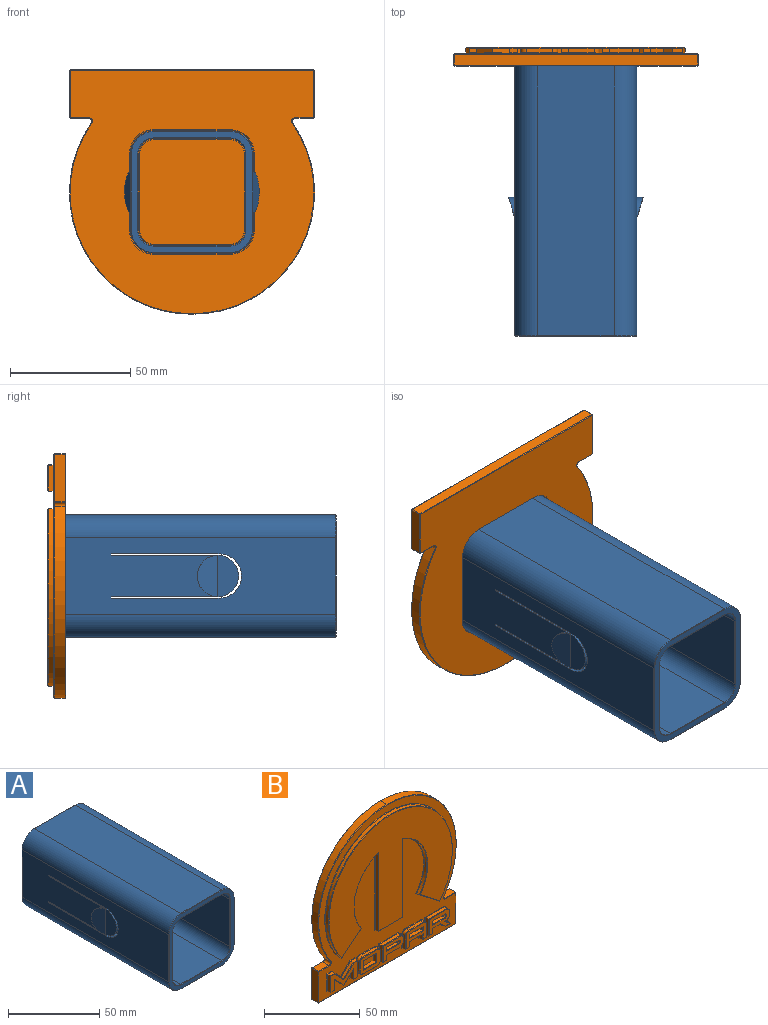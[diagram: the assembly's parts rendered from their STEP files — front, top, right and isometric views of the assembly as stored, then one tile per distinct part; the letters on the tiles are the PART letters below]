
ASSEMBLY  parts=2 mates=1
PART A: 72 faces, bbox 61x119.4x55.9 mm
  f0: cylinder r=8.57mm len=17.15mm, axis (1,0,0), area 0mm2, adj f6,f39
  f1: plane 17.15x8.58mm, normal (-1,0,0), area 115.4mm2, adj f23,f39
  f2: plane 113.79x31.75mm, normal (1,0,0), area 3296.9mm2, adj f9,f18,f29,f30,f31,f32,f33,f35
  f3: plane 17.15x8.58mm, normal (1,0,0), area 115.4mm2, adj f34,f38
  f4: plane 113.79x31.75mm, normal (0,0,1), area 3612.9mm2, adj f5,f18,f47,f63
  f5: cylinder r=9.53mm len=113.79mm, axis (0,1,0), area 1702.5mm2, adj f4,f6,f46,f62
  f6: plane 113.79x31.75mm, normal (-1,0,0), area 3296.9mm2, adj f0,f5,f7,f21,f22,f24,f25,f26
  f7: cylinder r=9.53mm len=113.79mm, axis (0,1,0), area 1702.5mm2, adj f6,f8,f42,f58
  f8: plane 113.79x31.75mm, normal (0,0,-1), area 3612.9mm2, adj f7,f9,f40,f56
  f9: cylinder r=9.53mm len=113.79mm, axis (0,1,0), area 1702.5mm2, adj f2,f8,f41,f57
  f10: cylinder r=6.35mm len=113.79mm, axis (0,1,0), area 1135mm2, adj f11,f17,f48,f64
  f11: plane 113.79x31.75mm, normal (-1,0,0), area 3527.8mm2, adj f10,f12,f29,f30,f31,f32,f33,f34
  f12: cylinder r=6.35mm len=113.79mm, axis (0,1,0), area 1135mm2, adj f11,f13,f52,f68
  f13: plane 113.79x31.75mm, normal (0,0,1), area 3612.9mm2, adj f12,f14,f54,f70
  f14: cylinder r=6.35mm len=113.79mm, axis (0,1,0), area 1135mm2, adj f13,f15,f55,f71
  f15: plane 113.79x31.75mm, normal (1,0,0), area 3527.8mm2, adj f14,f16,f21,f22,f23,f24,f25,f26
  f16: cylinder r=6.35mm len=113.79mm, axis (0,1,0), area 1135mm2, adj f15,f17,f51,f67
  f17: plane 113.79x31.75mm, normal (0,0,-1), area 3612.9mm2, adj f10,f16,f49,f65
  f18: cylinder r=9.53mm len=113.79mm, axis (0,1,0), area 1702.5mm2, adj f2,f4,f45,f61
  f19: plane 50.29x50.29mm, normal (0,-1,0), area 471.7mm2, adj f56,f57,f58,f59,f60,f61,f62,f63
  f20: plane 50.29x50.29mm, normal (0,1,0), area 471.7mm2, adj f40,f41,f42,f43,f44,f45,f46,f47
  f21: plane 3.18x0.64mm, normal (0,-1,0), area 2mm2, adj f6,f15,f22,f28
  f22: plane 44.45x3.18mm, normal (0,0,1), area 141.1mm2, adj f6,f15,f21,f23
  f23: cylinder r=8.57mm len=17.15mm, axis (1,0,0), area 85.6mm2, adj f1,f15,f22,f24
  f24: plane 44.45x3.18mm, normal (0,0,-1), area 141.1mm2, adj f6,f15,f23,f25
  f25: plane 3.18x0.64mm, normal (0,-1,0), area 2mm2, adj f6,f15,f24,f26
  f26: plane 44.45x3.18mm, normal (0,0,1), area 141.1mm2, adj f6,f15,f25,f27
  f27: cylinder r=9.22mm len=18.45mm, axis (1,0,0), area 95.6mm2, adj f6,f15,f26,f28
  f28: plane 44.45x3.18mm, normal (0,0,-1), area 141.1mm2, adj f6,f15,f21,f27
  f29: plane 44.45x3.18mm, normal (0,0,-1), area 141.1mm2, adj f2,f11,f30,f36
  f30: cylinder r=9.22mm len=18.45mm, axis (1,0,0), area 95.6mm2, adj f2,f11,f29,f31
  f31: plane 44.45x3.18mm, normal (0,0,1), area 141.1mm2, adj f2,f11,f30,f32
  f32: plane 3.18x0.64mm, normal (0,-1,0), area 2mm2, adj f2,f11,f31,f33
  f33: plane 44.45x3.18mm, normal (0,0,-1), area 141.1mm2, adj f2,f11,f32,f34
  f34: cylinder r=8.57mm len=17.15mm, axis (1,0,0), area 85.6mm2, adj f3,f11,f33,f35
  f35: plane 44.45x3.18mm, normal (0,0,1), area 141.1mm2, adj f2,f11,f34,f36
  f36: plane 3.18x0.64mm, normal (0,-1,0), area 2mm2, adj f2,f11,f29,f35
  f37: cylinder r=8.57mm len=17.15mm, axis (-1,0,0), area 0mm2, adj f2,f38
  f38: plane 22.22x13.65mm, normal (0.96,-0.28,0), area 120.4mm2, adj f3,f37
  f39: plane 22.22x13.65mm, normal (-0.96,-0.28,0), area 120.4mm2, adj f0,f1
  f40: plane 31.75x0.25mm, normal (0,0.71,-0.71), area 11.4mm2, adj f8,f20,f41,f42
  f41: cone r=9.53mm half-angle=45deg, axis (0,-1,0), area 5.3mm2, adj f9,f20,f40,f43
  f42: cone r=9.53mm half-angle=45deg, axis (0,-1,0), area 5.3mm2, adj f7,f20,f40,f44
  f43: plane 31.75x0.25mm, normal (0.71,0.71,0), area 11.4mm2, adj f2,f20,f41,f45
  f44: plane 31.75x0.25mm, normal (-0.71,0.71,0), area 11.4mm2, adj f6,f20,f42,f46
  f45: cone r=9.53mm half-angle=45deg, axis (0,-1,0), area 5.3mm2, adj f18,f20,f43,f47
  f46: cone r=9.53mm half-angle=45deg, axis (0,-1,0), area 5.3mm2, adj f5,f20,f44,f47
  f47: plane 31.75x0.25mm, normal (0,0.71,0.71), area 11.4mm2, adj f4,f20,f45,f46
  f48: cone r=6.6mm half-angle=45deg, axis (0,1,0), area 3.7mm2, adj f10,f20,f49,f50
  f49: plane 31.75x0.25mm, normal (0,0.71,-0.71), area 11.4mm2, adj f17,f20,f48,f51
  f50: plane 31.75x0.25mm, normal (-0.71,0.71,0), area 11.4mm2, adj f11,f20,f48,f52
  f51: cone r=6.6mm half-angle=45deg, axis (0,1,0), area 3.7mm2, adj f16,f20,f49,f53
  f52: cone r=6.6mm half-angle=45deg, axis (0,1,0), area 3.7mm2, adj f12,f20,f50,f54
  f53: plane 31.75x0.25mm, normal (0.71,0.71,0), area 11.4mm2, adj f15,f20,f51,f55
  f54: plane 31.75x0.25mm, normal (0,0.71,0.71), area 11.4mm2, adj f13,f20,f52,f55
  f55: cone r=6.6mm half-angle=45deg, axis (0,1,0), area 3.7mm2, adj f14,f20,f53,f54
  f56: plane 31.75x0.25mm, normal (0,-0.71,-0.71), area 11.4mm2, adj f8,f19,f57,f58
  f57: cone r=9.27mm half-angle=45deg, axis (0,1,0), area 5.3mm2, adj f9,f19,f56,f59
  f58: cone r=9.27mm half-angle=45deg, axis (0,1,0), area 5.3mm2, adj f7,f19,f56,f60
  f59: plane 31.75x0.25mm, normal (0.71,-0.71,0), area 11.4mm2, adj f2,f19,f57,f61
  f60: plane 31.75x0.25mm, normal (-0.71,-0.71,0), area 11.4mm2, adj f6,f19,f58,f62
  f61: cone r=9.27mm half-angle=45deg, axis (0,1,0), area 5.3mm2, adj f18,f19,f59,f63
  f62: cone r=9.27mm half-angle=45deg, axis (0,1,0), area 5.3mm2, adj f5,f19,f60,f63
  f63: plane 31.75x0.25mm, normal (0,-0.71,0.71), area 11.4mm2, adj f4,f19,f61,f62
  f64: cone r=6.35mm half-angle=45deg, axis (0,-1,0), area 3.7mm2, adj f10,f19,f65,f66
  f65: plane 31.75x0.25mm, normal (0,-0.71,-0.71), area 11.4mm2, adj f17,f19,f64,f67
  f66: plane 31.75x0.25mm, normal (-0.71,-0.71,0), area 11.4mm2, adj f11,f19,f64,f68
  f67: cone r=6.35mm half-angle=45deg, axis (0,-1,0), area 3.7mm2, adj f16,f19,f65,f69
  f68: cone r=6.35mm half-angle=45deg, axis (0,-1,0), area 3.7mm2, adj f12,f19,f66,f70
  f69: plane 31.75x0.25mm, normal (0.71,-0.71,0), area 11.4mm2, adj f15,f19,f67,f71
  f70: plane 31.75x0.25mm, normal (0,-0.71,0.71), area 11.4mm2, adj f13,f19,f68,f71
  f71: cone r=6.35mm half-angle=45deg, axis (0,-1,0), area 3.7mm2, adj f14,f19,f69,f70
PART B: 279 faces, bbox 101.9x7.6x101.6 mm
  f0: plane 101.38x101.09mm, normal (0,1,0), area 6348.8mm2, adj f110,f114,f115,f119,f123,f124,f128,f132
  f1: plane 101.38x101.09mm, normal (0,-1,0), area 4120.3mm2, adj f113,f117,f118,f122,f126,f127,f131,f134
  f2: plane 19.72x4.57mm, normal (-1,0,0), area 90.2mm2, adj f109,f115,f116,f117
  f3: plane 101.09x4.57mm, normal (0,0,-1), area 462.2mm2, adj f116,f124,f125,f126
  f4: plane 19.72x4.57mm, normal (1,0,0), area 90.2mm2, adj f125,f133,f134,f138
  f5: plane 7.75x4.57mm, normal (0,0,1), area 35.4mm2, adj f6,f132,f135,f138
  f6: cylinder r=1.14mm len=4.57mm, axis (0,-1,0), area 10.7mm2, adj f5,f7,f128,f131
  f7: cylinder r=50.6mm len=79.71mm, axis (0,-1,0), area 507mm2, adj f6,f8,f123,f127
  f8: cylinder r=50.59mm len=79.71mm, axis (0,-1,0), area 506.5mm2, adj f7,f9,f119,f122
  f9: cylinder r=1.21mm len=4.57mm, axis (0,-1,0), area 10.8mm2, adj f8,f10,f114,f118
  f10: plane 7.75x4.57mm, normal (0,0,1), area 35.4mm2, adj f9,f109,f110,f113
  f11: cylinder r=27.14mm len=41.92mm, axis (0,1,0), area 103.1mm2, adj f12,f18,f251,f259
  f12: plane 49.94x2.03mm, normal (-1,0,0), area 101.5mm2, adj f11,f13,f249,f257
  f13: plane 18.1x2.03mm, normal (0,0,-1), area 36.8mm2, adj f12,f14,f247,f255
  f14: plane 49.94x2.03mm, normal (1,0,0), area 101.5mm2, adj f13,f15,f248,f256
  f15: cylinder r=26.93mm len=41.92mm, axis (0,1,0), area 103.5mm2, adj f14,f16,f250,f258
  f16: plane 14.83x11.39mm, normal (-0.61,0,-0.79), area 38mm2, adj f15,f17,f252,f260
  f17: cylinder r=45.71mm len=91.43mm, axis (0,1,0), area 414.1mm2, adj f16,f18,f254,f262
  f18: plane 14.83x11.62mm, normal (0.62,0,-0.79), area 38.3mm2, adj f11,f17,f253,f261
  f19: plane 90.92x73.17mm, normal (0,-1,0), area 3840.9mm2, adj f255,f256,f257,f258,f259,f260,f261,f262
  f20: plane 10.61x2.03mm, normal (-1,0,0), area 21.6mm2, adj f21,f31,f199,f245
  f21: plane 3.08x2.03mm, normal (0,0,-1), area 6.3mm2, adj f20,f22,f200,f246
  f22: plane 6.64x2.03mm, normal (1,0,0), area 13.5mm2, adj f21,f23,f198,f244
  f23: plane 6.91x6.73mm, normal (-0.72,0,-0.7), area 19.6mm2, adj f22,f24,f196,f242
  f24: plane 7.1x6.91mm, normal (0.7,0,-0.72), area 20.1mm2, adj f23,f25,f194,f240
  f25: plane 6.64x2.03mm, normal (-1,0,0), area 13.5mm2, adj f24,f26,f192,f238
  f26: plane 3.07x2.03mm, normal (0,0,-1), area 6.2mm2, adj f25,f27,f190,f236
  f27: plane 10.61x2.03mm, normal (1,0,0), area 21.6mm2, adj f26,f28,f189,f235
  f28: plane 3.12x2.03mm, normal (0,0,1), area 6.3mm2, adj f27,f29,f191,f237
  f29: plane 7.05x6.86mm, normal (-0.7,0,0.72), area 20mm2, adj f28,f30,f193,f239
  f30: plane 6.86x6.68mm, normal (0.72,0,0.7), area 19.5mm2, adj f29,f31,f195,f241
  f31: plane 3.13x2.03mm, normal (0,0,1), area 6.4mm2, adj f20,f30,f197,f243
  f32: plane 19.47x10.27mm, normal (0,-1,0), area 99.2mm2, adj f189,f190,f191,f192,f193,f194,f195,f196
  f33: plane 6.36x2.03mm, normal (1,0,0), area 12.9mm2, adj f34,f44,f183,f229
  f34: cylinder r=2.09mm len=2.23mm, axis (0,1,0), area 6.9mm2, adj f33,f35,f181,f227
  f35: plane 10.69x2.03mm, normal (0,0,1), area 21.7mm2, adj f34,f36,f182,f228
  f36: cylinder r=2.11mm len=2.42mm, axis (0,1,0), area 7.4mm2, adj f35,f37,f184,f230
  f37: plane 6.36x2.03mm, normal (-1,0,0), area 12.9mm2, adj f36,f38,f186,f232
  f38: cylinder r=2.31mm len=2.42mm, axis (0,1,0), area 7.6mm2, adj f37,f39,f188,f234
  f39: plane 10.69x2.03mm, normal (0,0,-1), area 21.7mm2, adj f38,f44,f187,f233
  f40: plane 5.47x2.29mm, normal (1,0,0), area 12.5mm2, adj f41,f43,f46,f179
  f41: plane 9.25x2.29mm, normal (0,0,-1), area 21.1mm2, adj f40,f42,f46,f180
  f42: plane 5.47x2.29mm, normal (-1,0,0), area 12.5mm2, adj f41,f43,f46,f178
  f43: plane 9.25x2.29mm, normal (0,0,1), area 21.1mm2, adj f40,f42,f46,f177
  f44: cylinder r=2.23mm len=2.31mm, axis (0,1,0), area 7.3mm2, adj f33,f39,f185,f231
  f45: plane 14.83x10.27mm, normal (0,-1,0), area 90.4mm2, adj f177,f178,f179,f180,f181,f182,f183,f184
  f46: plane 9.25x5.47mm, normal (0,-1,0), area 50.6mm2, adj f40,f41,f42,f43
  f47: plane 13.6x2.03mm, normal (0,0,1), area 27.6mm2, adj f48,f56,f175,f225
  f48: plane 10.75x2.03mm, normal (-1,0,0), area 21.8mm2, adj f47,f49,f173,f223
  f49: plane 3.01x2.03mm, normal (0,0,-1), area 6.1mm2, adj f48,f50,f171,f221
  f50: plane 3.3x2.03mm, normal (1,0,0), area 6.7mm2, adj f49,f51,f172,f222
  f51: plane 10.59x2.03mm, normal (0,0,-1), area 21.5mm2, adj f50,f56,f174,f224
  f52: plane 2.29x1.9mm, normal (1,0,0), area 4.3mm2, adj f53,f55,f58,f167
  f53: plane 9.26x2.29mm, normal (0,0,-1), area 21.2mm2, adj f52,f54,f58,f169
  f54: cylinder r=1.41mm len=2.29mm, axis (0,1,0), area 4.8mm2, adj f53,f55,f58,f170
  f55: plane 9.26x2.29mm, normal (0,0,1), area 21.2mm2, adj f52,f54,f58,f168
  f56: cylinder r=4.16mm len=7.45mm, axis (0,1,0), area 18.7mm2, adj f47,f51,f176,f226
  f57: plane 15.4x10.24mm, normal (0,-1,0), area 87mm2, adj f167,f168,f169,f170,f171,f172,f173,f174
  f58: plane 9.62x1.9mm, normal (0,-1,0), area 18mm2, adj f52,f53,f54,f55
  f59: plane 2.29x2.16mm, normal (1,0,0), area 4.9mm2, adj f60,f72,f74,f155
  f60: plane 9.3x2.29mm, normal (0,0,-1), area 21.3mm2, adj f59,f61,f74,f156
  f61: plane 2.29x2.16mm, normal (-1,0,0), area 4.9mm2, adj f60,f72,f74,f154
  f62: plane 8.63x2.03mm, normal (-1,0,0), area 17.5mm2, adj f63,f71,f161,f215
  f63: plane 3.1x2.03mm, normal (0,0,-1), area 6.3mm2, adj f62,f64,f159,f213
  f64: plane 3.37x2.03mm, normal (1,0,0), area 6.8mm2, adj f63,f65,f157,f211
  f65: plane 9.44x2.03mm, normal (0,0,-1), area 19.2mm2, adj f64,f66,f158,f212
  f66: plane 3.37x2.03mm, normal (-1,0,0), area 6.8mm2, adj f65,f67,f160,f214
  f67: plane 2.96x2.03mm, normal (0,0,-1), area 6mm2, adj f66,f68,f162,f216
  f68: plane 8.63x2.03mm, normal (1,0,0), area 17.5mm2, adj f67,f69,f164,f218
  f69: cylinder r=2.31mm len=2.31mm, axis (0,1,0), area 7mm2, adj f68,f70,f166,f220
  f70: plane 10.67x2.03mm, normal (0,0,1), area 21.7mm2, adj f69,f71,f165,f219
  f71: cylinder r=2.15mm len=2.52mm, axis (0,1,0), area 7.6mm2, adj f62,f70,f163,f217
  f72: plane 9.3x2.29mm, normal (0,0,1), area 21.3mm2, adj f59,f61,f74,f153
  f73: plane 14.99x10.27mm, normal (0,-1,0), area 92.2mm2, adj f153,f154,f155,f156,f157,f158,f159,f160
  f74: plane 9.3x2.16mm, normal (0,-1,0), area 20.1mm2, adj f59,f60,f61,f72
  f75: plane 13.4x2.03mm, normal (0,0,1), area 27.2mm2, adj f76,f88,f151,f209
  f76: plane 10.75x2.03mm, normal (-1,0,0), area 21.8mm2, adj f75,f77,f149,f207
  f77: plane 3.13x2.03mm, normal (0,0,-1), area 6.4mm2, adj f76,f78,f147,f205
  f78: plane 3.37x2.03mm, normal (1,0,0), area 6.8mm2, adj f77,f79,f145,f203
  f79: plane 5.28x2.03mm, normal (0,0,-1), area 10.7mm2, adj f78,f80,f143,f201
  f80: plane 3.87x3.37mm, normal (-0.66,0,-0.75), area 10.4mm2, adj f79,f81,f144,f202
  f81: plane 4.23x2.03mm, normal (0,0,-1), area 8.6mm2, adj f80,f82,f146,f204
  f82: plane 4.23x3.37mm, normal (0.62,0,0.78), area 11mm2, adj f81,f83,f148,f206
  f83: plane 2.03x1.13mm, normal (0,0,-1), area 2.3mm2, adj f82,f88,f150,f208
  f84: plane 2.29x2.16mm, normal (1,0,0), area 4.9mm2, adj f85,f87,f90,f139
  f85: plane 9.03x2.29mm, normal (0,0,-1), area 20.6mm2, adj f84,f86,f90,f141
  f86: cylinder r=1.19mm len=2.29mm, axis (0,1,0), area 6.2mm2, adj f85,f87,f90,f142
  f87: plane 9.03x2.29mm, normal (0,0,1), area 20.6mm2, adj f84,f86,f90,f140
  f88: cylinder r=4.03mm len=7.38mm, axis (0,1,0), area 19mm2, adj f75,f83,f152,f210
  f89: plane 15.52x10.24mm, normal (0,-1,0), area 93.9mm2, adj f139,f140,f141,f142,f143,f144,f145,f146
  f90: plane 9.72x2.16mm, normal (0,-1,0), area 20.6mm2, adj f84,f85,f86,f87
  f91: cylinder r=6.1mm len=6.1mm, axis (0,1,0), area 15.8mm2, adj f92,f106,f107,f269
  f92: plane 31.75x1.65mm, normal (-1,0,0), area 52.4mm2, adj f91,f93,f107,f267
  f93: cylinder r=6.1mm len=6.1mm, axis (0,1,0), area 15.8mm2, adj f92,f94,f107,f265
  f94: plane 31.75x1.65mm, normal (0,0,-1), area 52.4mm2, adj f93,f95,f107,f263
  f95: cylinder r=6.1mm len=6.1mm, axis (0,1,0), area 15.8mm2, adj f94,f96,f107,f264
  f96: plane 31.75x1.65mm, normal (1,0,0), area 52.4mm2, adj f95,f97,f107,f266
  f97: cylinder r=6.1mm len=6.1mm, axis (0,1,0), area 15.8mm2, adj f96,f106,f107,f268
  f98: plane 31.75x1.65mm, normal (-1,0,0), area 52.4mm2, adj f99,f105,f107,f277
  f99: cylinder r=9.78mm len=9.78mm, axis (0,1,0), area 25.4mm2, adj f98,f100,f107,f275
  f100: plane 31.75x1.65mm, normal (0,0,1), area 52.4mm2, adj f99,f101,f107,f273
  f101: cylinder r=9.78mm len=9.78mm, axis (0,1,0), area 25.4mm2, adj f100,f102,f107,f271
  f102: plane 31.75x1.65mm, normal (1,0,0), area 52.4mm2, adj f101,f103,f107,f272
  f103: cylinder r=9.78mm len=9.78mm, axis (0,1,0), area 25.4mm2, adj f102,f104,f107,f274
  f104: plane 31.75x1.65mm, normal (0,0,-1), area 52.4mm2, adj f103,f105,f107,f276
  f105: cylinder r=9.78mm len=9.78mm, axis (0,1,0), area 25.4mm2, adj f98,f104,f107,f278
  f106: plane 31.75x1.65mm, normal (0,0,1), area 52.4mm2, adj f91,f97,f107,f270
  f107: plane 51.31x51.31mm, normal (0,1,0), area 651.4mm2, adj f91,f92,f93,f94,f95,f96,f97,f98
  f108: plane 43.43x43.43mm, normal (0,1,0), area 1857.2mm2, adj f263,f264,f265,f266,f267,f268,f269,f270
  f109: plane 4.57x0.25mm, normal (-0.71,0,0.71), area 1.6mm2, adj f2,f10,f111,f112
  f110: plane 7.75x0.25mm, normal (0,0.71,0.71), area 2.8mm2, adj f0,f10,f111,f114
  f111: plane 0.25x0.25mm, normal (-0.58,0.58,0.58), area 0.1mm2, adj f109,f110,f115
  f112: plane 0.25x0.25mm, normal (-0.58,-0.58,0.58), area 0.1mm2, adj f109,f113,f117
  f113: plane 7.75x0.25mm, normal (0,-0.71,0.71), area 2.8mm2, adj f1,f10,f112,f118
  f114: cone r=1.47mm half-angle=45deg, axis (0,1,0), area 0.9mm2, adj f0,f9,f110,f119
  f115: plane 19.72x0.25mm, normal (-0.71,0.71,0), area 7.1mm2, adj f0,f2,f111,f120
  f116: plane 4.57x0.25mm, normal (-0.71,0,-0.71), area 1.6mm2, adj f2,f3,f120,f121
  f117: plane 19.72x0.25mm, normal (-0.71,-0.71,0), area 7.1mm2, adj f1,f2,f112,f121
  f118: cone r=1.21mm half-angle=45deg, axis (0,-1,0), area 0.9mm2, adj f1,f9,f113,f122
  f119: cone r=50.59mm half-angle=45deg, axis (0,-1,0), area 39.7mm2, adj f0,f8,f114,f123
  f120: plane 0.25x0.25mm, normal (-0.58,0.58,-0.58), area 0.1mm2, adj f115,f116,f124
  f121: plane 0.25x0.25mm, normal (-0.58,-0.58,-0.58), area 0.1mm2, adj f116,f117,f126
  f122: cone r=50.34mm half-angle=45deg, axis (0,1,0), area 39.7mm2, adj f1,f8,f118,f127
  f123: cone r=50.6mm half-angle=45deg, axis (0,-1,0), area 39.7mm2, adj f0,f7,f119,f128
  f124: plane 101.09x0.25mm, normal (0,0.71,-0.71), area 36.3mm2, adj f0,f3,f120,f129
  f125: plane 4.57x0.25mm, normal (0.71,0,-0.71), area 1.6mm2, adj f3,f4,f129,f130
  f126: plane 101.09x0.25mm, normal (0,-0.71,-0.71), area 36.3mm2, adj f1,f3,f121,f130
  f127: cone r=50.35mm half-angle=45deg, axis (0,1,0), area 39.7mm2, adj f1,f7,f122,f131
  f128: cone r=1.4mm half-angle=45deg, axis (0,1,0), area 0.9mm2, adj f0,f6,f123,f132
  f129: plane 0.25x0.25mm, normal (0.58,0.58,-0.58), area 0.1mm2, adj f124,f125,f133
  f130: plane 0.25x0.25mm, normal (0.58,-0.58,-0.58), area 0.1mm2, adj f125,f126,f134
  f131: cone r=1.14mm half-angle=45deg, axis (0,-1,0), area 0.9mm2, adj f1,f6,f127,f135
  f132: plane 7.75x0.25mm, normal (0,0.71,0.71), area 2.8mm2, adj f0,f5,f128,f136
  f133: plane 19.72x0.25mm, normal (0.71,0.71,0), area 7.1mm2, adj f0,f4,f129,f136
  f134: plane 19.72x0.25mm, normal (0.71,-0.71,0), area 7.1mm2, adj f1,f4,f130,f137
  f135: plane 7.75x0.25mm, normal (0,-0.71,0.71), area 2.8mm2, adj f1,f5,f131,f137
  f136: plane 0.25x0.25mm, normal (0.58,0.58,0.58), area 0.1mm2, adj f132,f133,f138
  f137: plane 0.25x0.25mm, normal (0.58,-0.58,0.58), area 0.1mm2, adj f134,f135,f138
  f138: plane 4.57x0.25mm, normal (0.71,0,0.71), area 1.6mm2, adj f4,f5,f136,f137
  f139: plane 2.67x0.25mm, normal (0.71,-0.71,0), area 0.9mm2, adj f84,f89,f140,f141
  f140: plane 9.34x0.26mm, normal (0,-0.71,0.71), area 3.3mm2, adj f87,f89,f139,f142
  f141: plane 9.34x0.26mm, normal (0,-0.71,-0.71), area 3.3mm2, adj f85,f89,f139,f142
  f142: cone r=1.19mm half-angle=45deg, axis (0,-1,0), area 1.1mm2, adj f86,f89,f140,f141
  f143: plane 5.63x0.25mm, normal (0,-0.71,-0.71), area 2mm2, adj f79,f89,f144,f145
  f144: plane 3.96x3.62mm, normal (-0.46,-0.71,-0.53), area 1.8mm2, adj f80,f89,f143,f146
  f145: plane 3.62x0.25mm, normal (0.71,-0.71,0), area 1.2mm2, adj f78,f89,f143,f147
  f146: plane 4.23x0.25mm, normal (0,-0.71,-0.71), area 1.4mm2, adj f81,f89,f144,f148
  f147: plane 3.13x0.25mm, normal (0,-0.71,-0.71), area 1mm2, adj f77,f89,f145,f149
  f148: plane 4.96x3.62mm, normal (0.44,-0.71,0.55), area 1.9mm2, adj f82,f89,f146,f150
  f149: plane 10.75x0.25mm, normal (-0.71,-0.71,0), area 3.8mm2, adj f76,f89,f147,f151
  f150: plane 1.86x0.26mm, normal (0,-0.71,-0.71), area 0.5mm2, adj f83,f89,f148,f152
  f151: plane 13.4x0.26mm, normal (0,-0.71,0.71), area 4.8mm2, adj f75,f89,f149,f152
  f152: cone r=3.77mm half-angle=45deg, axis (0,1,0), area 3.2mm2, adj f88,f89,f150,f151
  f153: plane 9.81x0.25mm, normal (0,-0.71,0.71), area 3.4mm2, adj f72,f73,f154,f155
  f154: plane 2.67x0.25mm, normal (-0.71,-0.71,0), area 0.9mm2, adj f61,f73,f153,f156
  f155: plane 2.67x0.25mm, normal (0.71,-0.71,0), area 0.9mm2, adj f59,f73,f153,f156
  f156: plane 9.81x0.25mm, normal (0,-0.71,-0.71), area 3.4mm2, adj f60,f73,f154,f155
  f157: plane 3.62x0.25mm, normal (0.71,-0.71,0), area 1.2mm2, adj f64,f73,f158,f159
  f158: plane 9.95x0.25mm, normal (0,-0.71,-0.71), area 3.5mm2, adj f65,f73,f157,f160
  f159: plane 3.1x0.25mm, normal (0,-0.71,-0.71), area 1mm2, adj f63,f73,f157,f161
  f160: plane 3.62x0.25mm, normal (-0.71,-0.71,0), area 1.2mm2, adj f66,f73,f158,f162
  f161: plane 8.63x0.25mm, normal (-0.71,-0.71,0), area 3.1mm2, adj f62,f73,f159,f163
  f162: plane 2.96x0.25mm, normal (0,-0.71,-0.71), area 1mm2, adj f67,f73,f160,f164
  f163: cone r=1.9mm half-angle=45deg, axis (0,1,0), area 1.3mm2, adj f71,f73,f161,f165
  f164: plane 8.63x0.25mm, normal (0.71,-0.71,0), area 3.1mm2, adj f68,f73,f162,f166
  f165: plane 10.69x0.26mm, normal (0,-0.71,0.71), area 3.8mm2, adj f70,f73,f163,f166
  f166: cone r=2.06mm half-angle=45deg, axis (0,1,0), area 1.2mm2, adj f69,f73,f164,f165
  f167: plane 2.4x0.25mm, normal (0.71,-0.71,0), area 0.8mm2, adj f52,f57,f168,f169
  f168: plane 9.62x0.26mm, normal (0,-0.71,0.71), area 3.4mm2, adj f55,f57,f167,f170
  f169: plane 9.62x0.26mm, normal (0,-0.71,-0.71), area 3.4mm2, adj f53,f57,f167,f170
  f170: cone r=1.41mm half-angle=45deg, axis (0,-1,0), area 0.9mm2, adj f54,f57,f168,f169
  f171: plane 3.01x0.25mm, normal (0,-0.71,-0.71), area 1mm2, adj f49,f57,f172,f173
  f172: plane 3.55x0.25mm, normal (0.71,-0.71,0), area 1.2mm2, adj f50,f57,f171,f174
  f173: plane 10.75x0.25mm, normal (-0.71,-0.71,0), area 3.8mm2, adj f48,f57,f171,f175
  f174: plane 10.85x0.26mm, normal (0,-0.71,-0.71), area 3.8mm2, adj f51,f57,f172,f176
  f175: plane 13.61x0.26mm, normal (0,-0.71,0.71), area 4.8mm2, adj f47,f57,f173,f176
  f176: cone r=3.91mm half-angle=45deg, axis (0,1,0), area 3.2mm2, adj f56,f57,f174,f175
  f177: plane 9.76x0.25mm, normal (0,-0.71,0.71), area 3.4mm2, adj f43,f45,f178,f179
  f178: plane 5.98x0.25mm, normal (-0.71,-0.71,0), area 2.1mm2, adj f42,f45,f177,f180
  f179: plane 5.98x0.25mm, normal (0.71,-0.71,0), area 2.1mm2, adj f40,f45,f177,f180
  f180: plane 9.76x0.25mm, normal (0,-0.71,-0.71), area 3.4mm2, adj f41,f45,f178,f179
  f181: cone r=1.83mm half-angle=45deg, axis (0,1,0), area 1.2mm2, adj f34,f45,f182,f183
  f182: plane 10.72x0.25mm, normal (0,-0.71,0.71), area 3.8mm2, adj f35,f45,f181,f184
  f183: plane 6.36x0.25mm, normal (0.71,-0.71,0), area 2.3mm2, adj f33,f45,f181,f185
  f184: cone r=1.85mm half-angle=45deg, axis (0,1,0), area 1.2mm2, adj f36,f45,f182,f186
  f185: cone r=1.97mm half-angle=45deg, axis (0,1,0), area 1.2mm2, adj f44,f45,f183,f187
  f186: plane 6.36x0.25mm, normal (-0.71,-0.71,0), area 2.3mm2, adj f37,f45,f184,f188
  f187: plane 10.7x0.25mm, normal (0,-0.71,-0.71), area 3.8mm2, adj f39,f45,f185,f188
  f188: cone r=2.05mm half-angle=45deg, axis (0,1,0), area 1.3mm2, adj f38,f45,f186,f187
  f189: plane 10.61x0.25mm, normal (0.71,-0.71,0), area 3.7mm2, adj f27,f32,f190,f191
  f190: plane 3.07x0.25mm, normal (0,-0.71,-0.71), area 1mm2, adj f26,f32,f189,f192
  f191: plane 3.12x0.25mm, normal (0,-0.71,0.71), area 1.1mm2, adj f28,f32,f189,f193
  f192: plane 7.24x0.25mm, normal (-0.71,-0.71,0), area 2.4mm2, adj f25,f32,f190,f194
  f193: plane 7.22x7.15mm, normal (-0.49,-0.71,0.51), area 3.6mm2, adj f29,f32,f191,f195
  f194: plane 7.52x7.35mm, normal (0.49,-0.71,-0.51), area 3.6mm2, adj f24,f32,f192,f196
  f195: plane 7.22x6.79mm, normal (0.51,-0.71,0.49), area 3.5mm2, adj f30,f32,f193,f197
  f196: plane 7.54x6.99mm, normal (-0.51,-0.71,-0.49), area 3.5mm2, adj f23,f32,f194,f198
  f197: plane 3.13x0.25mm, normal (0,-0.71,0.71), area 1.1mm2, adj f31,f32,f195,f199
  f198: plane 7.26x0.25mm, normal (0.71,-0.71,0), area 2.5mm2, adj f22,f32,f196,f200
  f199: plane 10.61x0.25mm, normal (-0.71,-0.71,0), area 3.7mm2, adj f20,f32,f197,f200
  f200: plane 3.08x0.25mm, normal (0,-0.71,-0.71), area 1mm2, adj f21,f32,f198,f199
  f201: plane 5.28x0.25mm, normal (0,-0.71,-0.71), area 1.8mm2, adj f1,f79,f202,f203
  f202: plane 3.96x3.62mm, normal (-0.46,-0.71,-0.53), area 1.8mm2, adj f1,f80,f201,f204
  f203: plane 3.62x0.25mm, normal (0.71,-0.71,0), area 1.2mm2, adj f1,f78,f201,f205
  f204: plane 5.06x0.25mm, normal (0,-0.71,-0.71), area 1.7mm2, adj f1,f81,f202,f206
  f205: plane 3.64x0.25mm, normal (0,-0.71,-0.71), area 1.2mm2, adj f1,f77,f203,f207
  f206: plane 4.96x3.62mm, normal (0.44,-0.71,0.55), area 1.9mm2, adj f1,f82,f204,f208
  f207: plane 11.25x0.25mm, normal (-0.71,-0.71,0), area 4mm2, adj f1,f76,f205,f209
  f208: plane 1.18x0.26mm, normal (0,-0.71,-0.71), area 0.3mm2, adj f1,f83,f206,f210
  f209: plane 13.7x0.26mm, normal (0,-0.71,0.71), area 4.9mm2, adj f1,f75,f207,f210
  f210: cone r=4.03mm half-angle=45deg, axis (0,1,0), area 3.5mm2, adj f1,f88,f208,f209
  f211: plane 3.62x0.25mm, normal (0.71,-0.71,0), area 1.2mm2, adj f1,f64,f212,f213
  f212: plane 9.44x0.25mm, normal (0,-0.71,-0.71), area 3.3mm2, adj f1,f65,f211,f214
  f213: plane 3.61x0.25mm, normal (0,-0.71,-0.71), area 1.2mm2, adj f1,f63,f211,f215
  f214: plane 3.62x0.25mm, normal (-0.71,-0.71,0), area 1.2mm2, adj f1,f66,f212,f216
  f215: plane 8.88x0.25mm, normal (-0.71,-0.71,0), area 3.1mm2, adj f1,f62,f213,f217
  f216: plane 3.46x0.25mm, normal (0,-0.71,-0.71), area 1.2mm2, adj f1,f67,f214,f218
  f217: cone r=2.15mm half-angle=45deg, axis (0,1,0), area 1.4mm2, adj f1,f71,f215,f219
  f218: plane 8.89x0.25mm, normal (0.71,-0.71,0), area 3.1mm2, adj f1,f68,f216,f220
  f219: plane 10.67x0.25mm, normal (0,-0.71,0.71), area 3.8mm2, adj f1,f70,f217,f220
  f220: cone r=2.31mm half-angle=45deg, axis (0,1,0), area 1.3mm2, adj f1,f69,f218,f219
  f221: plane 3.52x0.25mm, normal (0,-0.71,-0.71), area 1.2mm2, adj f1,f49,f222,f223
  f222: plane 3.55x0.25mm, normal (0.71,-0.71,0), area 1.2mm2, adj f1,f50,f221,f224
  f223: plane 11.25x0.25mm, normal (-0.71,-0.71,0), area 4mm2, adj f1,f48,f221,f225
  f224: plane 10.65x0.26mm, normal (0,-0.71,-0.71), area 3.8mm2, adj f1,f51,f222,f226
  f225: plane 13.92x0.26mm, normal (0,-0.71,0.71), area 4.9mm2, adj f1,f47,f223,f226
  f226: cone r=4.16mm half-angle=45deg, axis (0,1,0), area 3.4mm2, adj f1,f56,f224,f225
  f227: cone r=2.09mm half-angle=45deg, axis (0,1,0), area 1.3mm2, adj f1,f34,f228,f229
  f228: plane 10.69x0.25mm, normal (0,-0.71,0.71), area 3.8mm2, adj f1,f35,f227,f230
  f229: plane 6.36x0.25mm, normal (0.71,-0.71,0), area 2.3mm2, adj f1,f33,f227,f231
  f230: cone r=2.11mm half-angle=45deg, axis (0,1,0), area 1.4mm2, adj f1,f36,f228,f232
  f231: cone r=2.23mm half-angle=45deg, axis (0,1,0), area 1.4mm2, adj f1,f44,f229,f233
  f232: plane 6.36x0.25mm, normal (-0.71,-0.71,0), area 2.3mm2, adj f1,f37,f230,f234
  f233: plane 10.69x0.25mm, normal (0,-0.71,-0.71), area 3.8mm2, adj f1,f39,f231,f234
  f234: cone r=2.31mm half-angle=45deg, axis (0,1,0), area 1.4mm2, adj f1,f38,f232,f233
  f235: plane 11.12x0.25mm, normal (0.71,-0.71,0), area 3.9mm2, adj f1,f27,f236,f237
  f236: plane 3.58x0.25mm, normal (0,-0.71,-0.71), area 1.2mm2, adj f1,f26,f235,f238
  f237: plane 3.48x0.25mm, normal (0,-0.71,0.71), area 1.2mm2, adj f1,f28,f235,f239
  f238: plane 6.89x0.25mm, normal (-0.71,-0.71,0), area 2.3mm2, adj f1,f25,f236,f240
  f239: plane 7.11x7.05mm, normal (-0.49,-0.71,0.51), area 3.5mm2, adj f1,f29,f237,f241
  f240: plane 7.27x7.11mm, normal (0.49,-0.71,-0.51), area 3.5mm2, adj f1,f24,f238,f242
  f241: plane 7.11x6.68mm, normal (0.51,-0.71,0.49), area 3.4mm2, adj f1,f30,f239,f243
  f242: plane 7.27x6.73mm, normal (-0.51,-0.71,-0.49), area 3.4mm2, adj f1,f23,f240,f244
  f243: plane 3.49x0.25mm, normal (0,-0.71,0.71), area 1.2mm2, adj f1,f31,f241,f245
  f244: plane 6.89x0.25mm, normal (0.71,-0.71,0), area 2.3mm2, adj f1,f22,f242,f246
  f245: plane 11.12x0.25mm, normal (-0.71,-0.71,0), area 3.9mm2, adj f1,f20,f243,f246
  f246: plane 3.58x0.25mm, normal (0,-0.71,-0.71), area 1.2mm2, adj f1,f21,f244,f245
  f247: plane 18.61x0.25mm, normal (0,-0.71,-0.71), area 6.6mm2, adj f1,f13,f248,f249
  f248: plane 50.2x0.26mm, normal (0.71,-0.71,0), area 17.9mm2, adj f1,f14,f247,f250
  f249: plane 50.2x0.26mm, normal (-0.71,-0.71,0), area 17.9mm2, adj f1,f12,f247,f251
  f250: cone r=26.68mm half-angle=45deg, axis (0,-1,0), area 18.2mm2, adj f1,f15,f248,f252
  f251: cone r=26.89mm half-angle=45deg, axis (0,-1,0), area 18.1mm2, adj f1,f11,f249,f253
  f252: plane 15.24x11.75mm, normal (-0.43,-0.71,-0.56), area 6.8mm2, adj f1,f16,f250,f254
  f253: plane 15.23x11.98mm, normal (0.44,-0.71,-0.56), area 6.9mm2, adj f1,f18,f251,f254
  f254: cone r=45.71mm half-angle=45deg, axis (0,1,0), area 73.5mm2, adj f1,f17,f252,f253
  f255: plane 18.1x0.25mm, normal (0,-0.71,-0.71), area 6.4mm2, adj f13,f19,f256,f257
  f256: plane 50.3x0.26mm, normal (0.71,-0.71,0), area 18mm2, adj f14,f19,f255,f258
  f257: plane 50.3x0.26mm, normal (-0.71,-0.71,0), area 18mm2, adj f12,f19,f255,f259
  f258: cone r=26.93mm half-angle=45deg, axis (0,-1,0), area 18.4mm2, adj f15,f19,f256,f260
  f259: cone r=27.14mm half-angle=45deg, axis (0,-1,0), area 18.3mm2, adj f11,f19,f257,f261
  f260: plane 14.84x11.44mm, normal (-0.43,-0.71,-0.56), area 6.6mm2, adj f16,f19,f258,f262
  f261: plane 14.83x11.67mm, normal (0.44,-0.71,-0.56), area 6.7mm2, adj f18,f19,f259,f262
  f262: cone r=45.46mm half-angle=45deg, axis (0,1,0), area 72.9mm2, adj f17,f19,f260,f261
  f263: plane 31.75x0.25mm, normal (0,0.71,-0.71), area 11.4mm2, adj f94,f108,f264,f265
  f264: cone r=5.84mm half-angle=45deg, axis (0,-1,0), area 3.4mm2, adj f95,f108,f263,f266
  f265: cone r=5.84mm half-angle=45deg, axis (0,-1,0), area 3.4mm2, adj f93,f108,f263,f267
  f266: plane 31.75x0.25mm, normal (0.71,0.71,0), area 11.4mm2, adj f96,f108,f264,f268
  f267: plane 31.75x0.25mm, normal (-0.71,0.71,0), area 11.4mm2, adj f92,f108,f265,f269
  f268: cone r=5.84mm half-angle=45deg, axis (0,-1,0), area 3.4mm2, adj f97,f108,f266,f270
  f269: cone r=5.84mm half-angle=45deg, axis (0,-1,0), area 3.4mm2, adj f91,f108,f267,f270
  f270: plane 31.75x0.25mm, normal (0,0.71,0.71), area 11.4mm2, adj f106,f108,f268,f269
  f271: cone r=9.78mm half-angle=45deg, axis (0,1,0), area 5.6mm2, adj f0,f101,f272,f273
  f272: plane 31.75x0.25mm, normal (0.71,0.71,0), area 11.4mm2, adj f0,f102,f271,f274
  f273: plane 31.75x0.25mm, normal (0,0.71,0.71), area 11.4mm2, adj f0,f100,f271,f275
  f274: cone r=9.78mm half-angle=45deg, axis (0,1,0), area 5.6mm2, adj f0,f103,f272,f276
  f275: cone r=9.78mm half-angle=45deg, axis (0,1,0), area 5.6mm2, adj f0,f99,f273,f277
  f276: plane 31.75x0.25mm, normal (0,0.71,-0.71), area 11.4mm2, adj f0,f104,f274,f278
  f277: plane 31.75x0.25mm, normal (-0.71,0.71,0), area 11.4mm2, adj f0,f98,f275,f278
  f278: cone r=9.78mm half-angle=45deg, axis (0,1,0), area 5.6mm2, adj f0,f105,f276,f277
PLACE A t=(-45.37,-53.03,45.13)mm
PLACE B rot(axis=(1,0,0),180deg) t=(-42.54,-49.85,80.37)mm
MATE fastened B.f107 <-> A.f20  axis (0,-1,0) through (-45.37,-53.03,45.13)mm
